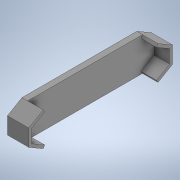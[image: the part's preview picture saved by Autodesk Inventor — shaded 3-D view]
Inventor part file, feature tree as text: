
AUTODESK INVENTOR PART (.ipt)
format: ipt  version: 2020 (Build 240168000, 168)  size: 139,264 bytes
history: native  units: in
note: dims shown in document units (in); Inventor stores cm internally (conversion verified against a paired STEP export)
features: extrude x2, sketch x2
ambient origin geometry x8: Origin, YZ Plane, XZ Plane, XY Plane, X Axis, Y Axis, Z Axis, Center Point
bodies: Solid1 (feature_tree)
feature tree (4):
  extrude  "Extrusion1"  Depth=5.9055in
  extrude  "Extrusion2"  TaperAngle=0.0deg  [1 undecoded]
  sketch  "Sketch1"  dims[d0=1.378in d1=5.9055in]
  sketch  "Sketch2"  dims[d2=0.2362in d3=0.0in d4=0.1181in d5=0.6378in d6=0.0in d7=0.1181in]
note: 1 required parameter value undecoded (feature->parameter linkage not recoverable at this tier; creation-order binding heuristic only, values carry confidence <= 0.55)
